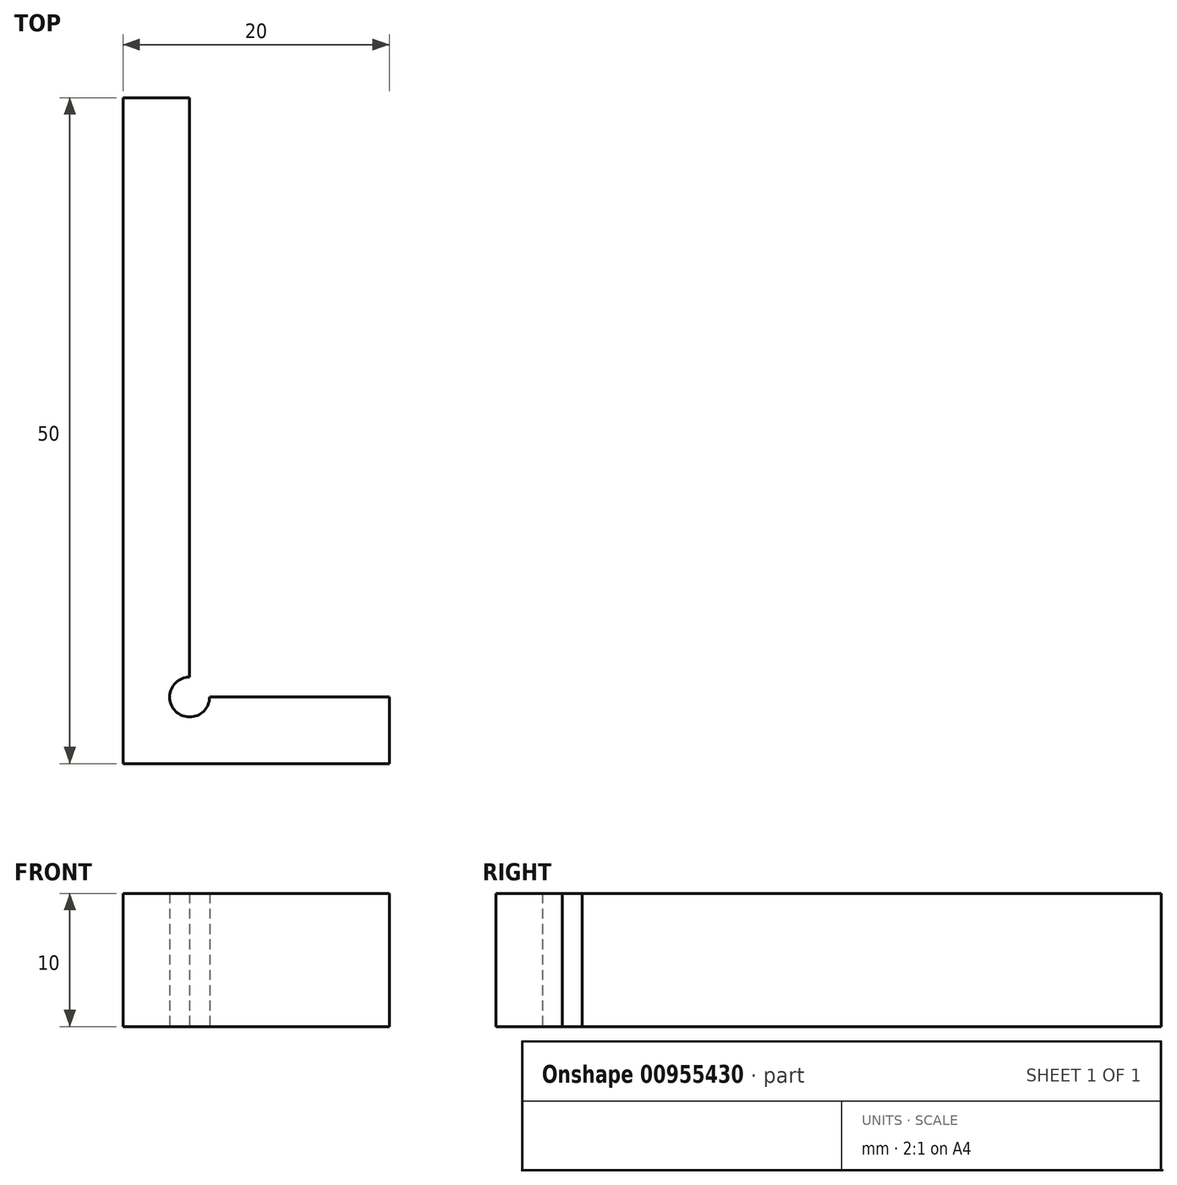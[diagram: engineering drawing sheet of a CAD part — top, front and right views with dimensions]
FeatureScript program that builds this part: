
annotation { "Feature Type Name" : "Feature", "Feature Type Description" : "" }
export const myFeature = defineFeature(function(context is Context, id is Id, definition is map)
    precondition{}
    {
        {
            var Q0;
            Q0=qCreatedBy(makeId("Top.planeOp"),FACE);
            var sketch = newSketch(context, id + "F0", { "sketchPlane" : qUnion([Q0])});
            skLineSegment(sketch, "E0", {"start": v(-4.78, 33.26) * mm, "end": v(-9.78, 33.26) * mm});
            skLineSegment(sketch, "E1", {"start": v(-9.78, 33.26) * mm, "end": v(-9.78, -16.74) * mm});
            skLineSegment(sketch, "E2", {"start": v(-9.78, -16.74) * mm, "end": v(10.22, -16.74) * mm});
            skLineSegment(sketch, "E3", {"start": v(10.22, -16.74) * mm, "end": v(10.22, -11.74) * mm});
            skLineSegment(sketch, "E4", {"start": v(10.22, -11.74) * mm, "end": v(-3.28, -11.74) * mm});
            skLineSegment(sketch, "E5", {"start": v(-4.78, -10.24) * mm, "end": v(-4.78, 33.26) * mm});
            skArc(sketch, "E6", {"start": v(-4.78, -10.24) * mm, "mid": v(-5.84, -12.8) * mm, "end": v(-3.28, -11.74) * mm});
            skSolve(sketch);
        }
        {
            var Q0;
            Q0 = qSketchRegion(id + "F0", true);
            extrude(context, id + "F1", {"entities" : qUnion([Q0]), "depth" : 10 * mm, "offsetDistance" : 25 * mm});
        }
    });
